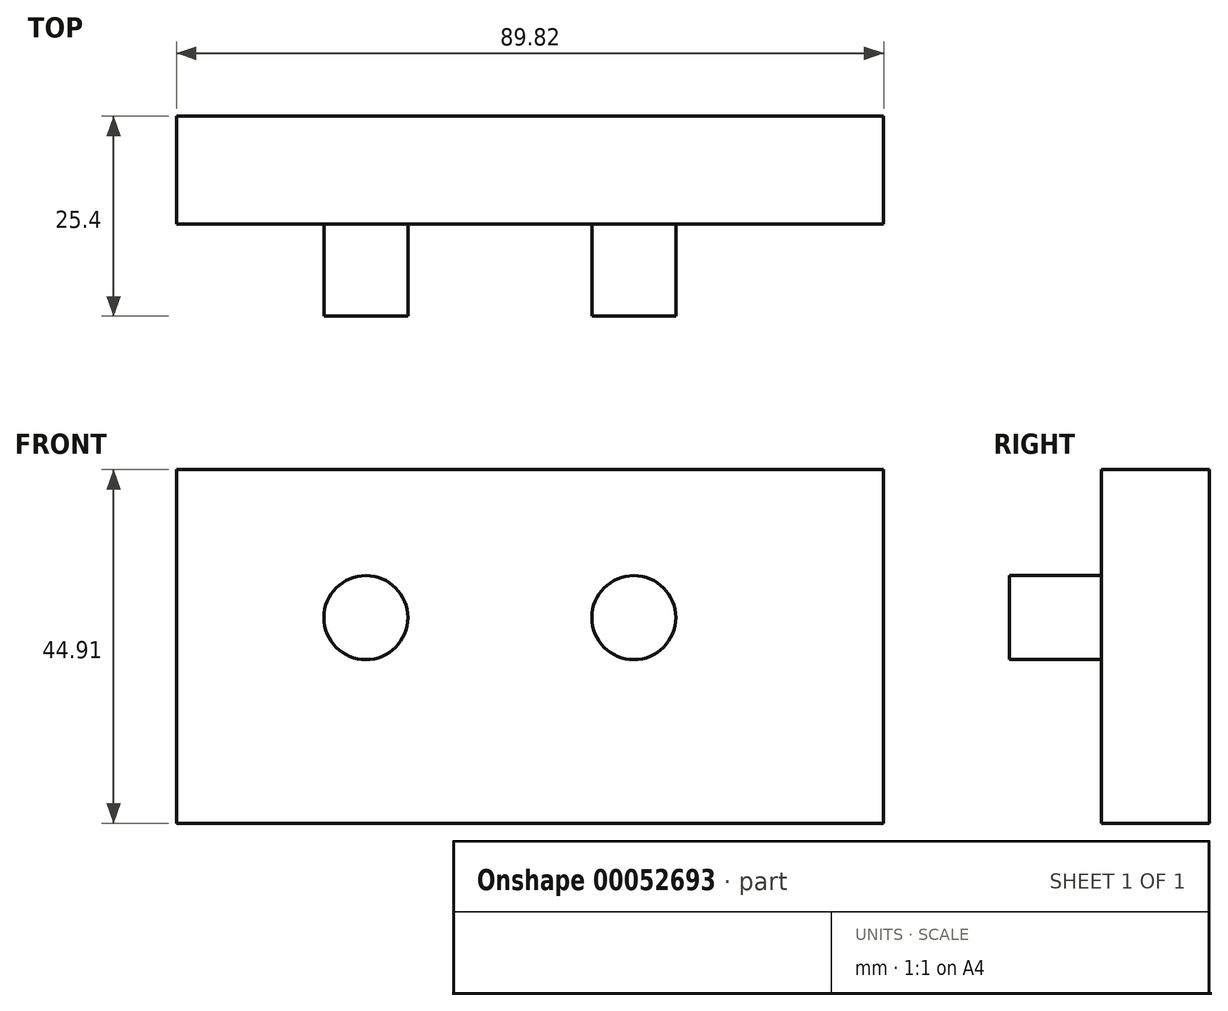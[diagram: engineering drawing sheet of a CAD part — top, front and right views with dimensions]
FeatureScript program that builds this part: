
annotation { "Feature Type Name" : "Feature", "Feature Type Description" : "" }
export const myFeature = defineFeature(function(context is Context, id is Id, definition is map)
    precondition{}
    {
        {
            var Q0;
            Q0=qCreatedBy(makeId("Front.planeOp"),FACE);
            var sketch = newSketch(context, id + "F0", { "sketchPlane" : qUnion([Q0])});
            skLineSegment(sketch, "E0.bottom", {"start": v(-41.06, 18.79) * mm, "end": v(48.76, 18.79) * mm});
            skLineSegment(sketch, "E0.top", {"start": v(-41.06, -26.12) * mm, "end": v(48.76, -26.12) * mm});
            skLineSegment(sketch, "E0.left", {"start": v(-41.06, 18.79) * mm, "end": v(-41.06, -26.12) * mm});
            skLineSegment(sketch, "E0.right", {"start": v(48.76, 18.79) * mm, "end": v(48.76, -26.12) * mm});
            skLineSegment(sketch, "E1", {"start": v(-17.02, 8.16) * mm, "end": v(-17.02, -13.84) * mm, "construction": true});
            skLineSegment(sketch, "E2", {"start": v(17.02, 6.5) * mm, "end": v(17.02, -12.92) * mm, "construction": true});
            skCircle(sketch, "E3", {"center": v(-17.02, 0) * mm, "radius": 5.33 * mm});
            skCircle(sketch, "E4", {"center": v(17.02, 0) * mm, "radius": 5.33 * mm});
            skSolve(sketch);
        }
        {
            var Q0;
            Q0=makeQuery(id+"F0.imprint","IMPRINT",FACE,{"disambiguationData":[TD([[makeQuery(id+"F0.imprint","IMPRINT",EDGE,{"derivedFrom":sQuery(id+"F0.wireOp",EDGE,"E0.bottom")}),-1.0]])]});
            var Q1;
            Q1=makeQuery(id+"F0.imprint","IMPRINT",FACE,{"disambiguationData":[TD([[makeQuery(id+"F0.imprint","IMPRINT",EDGE,{"derivedFrom":sQuery(id+"F0.wireOp",EDGE,"E3")}),1.0]])]});
            var Q2;
            Q2=makeQuery(id+"F0.imprint","IMPRINT",FACE,{"disambiguationData":[TD([[makeQuery(id+"F0.imprint","IMPRINT",EDGE,{"derivedFrom":sQuery(id+"F0.wireOp",EDGE,"E4")}),1.0]])]});
            extrude(context, id + "F1", {"entities" : qUnion([Q0, Q1, Q2]), "depth" : 13.72 * mm});
        }
        {
            var Q0;
            Q0=makeQuery(id+"F0.imprint","IMPRINT",FACE,{"disambiguationData":[TD([[makeQuery(id+"F0.imprint","IMPRINT",EDGE,{"derivedFrom":sQuery(id+"F0.wireOp",EDGE,"E4")}),1.0]])]});
            var Q1;
            Q1=makeQuery(id+"F0.imprint","IMPRINT",FACE,{"disambiguationData":[TD([[makeQuery(id+"F0.imprint","IMPRINT",EDGE,{"derivedFrom":sQuery(id+"F0.wireOp",EDGE,"E3")}),1.0]])]});
            extrude(context, id + "F2", {"entities" : qUnion([Q0, Q1]), "operationType" : NewBodyOperationType.ADD, "depth" : 25.4 * mm});
        }
    });
